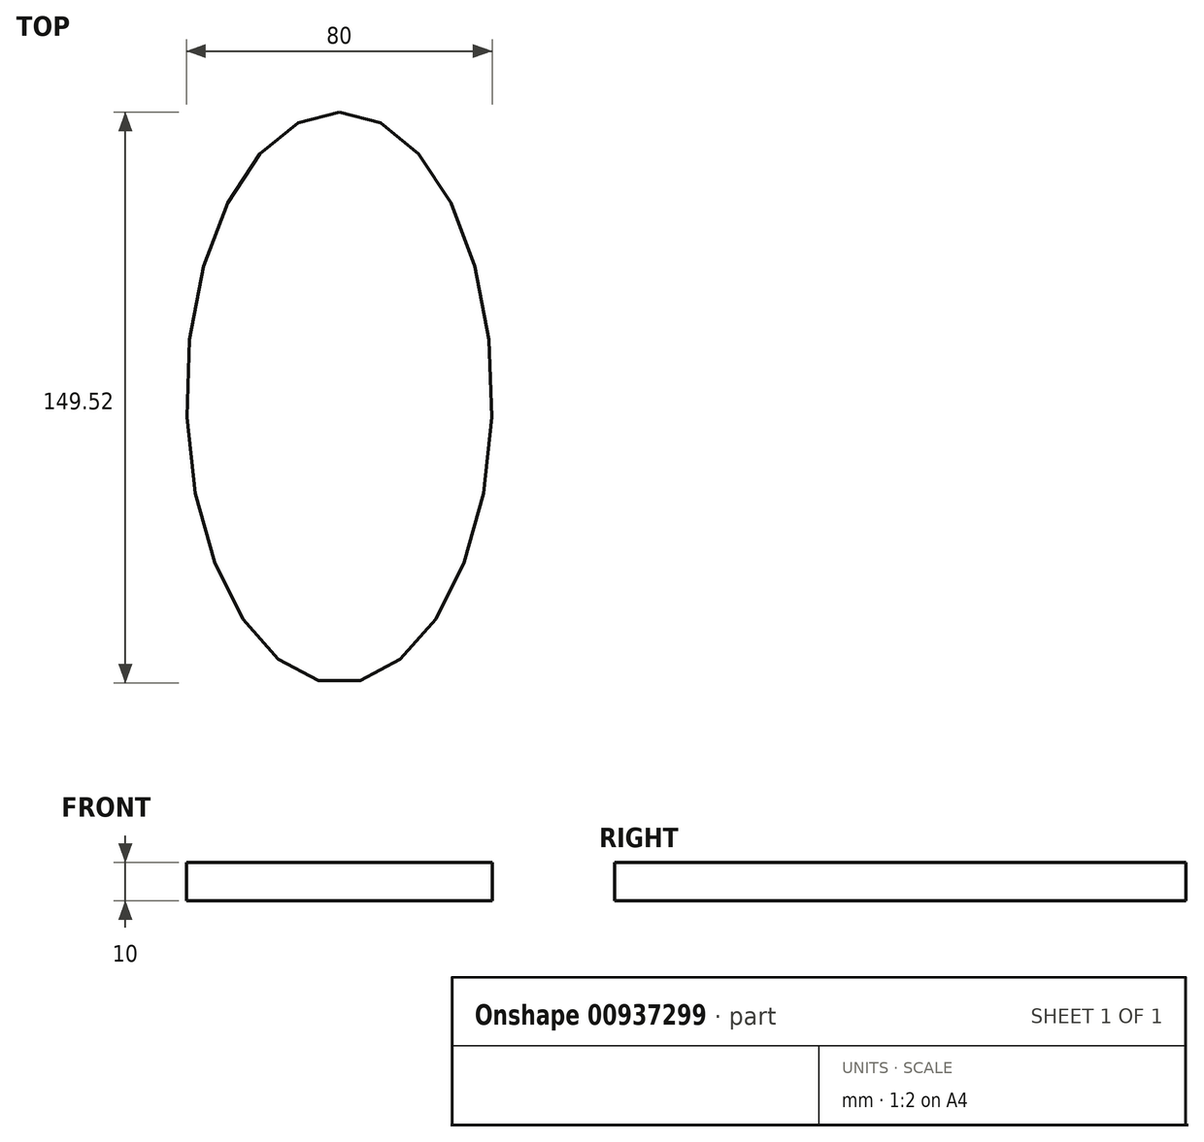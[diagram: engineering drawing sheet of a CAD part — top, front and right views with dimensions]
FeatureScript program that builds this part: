
annotation { "Feature Type Name" : "Feature", "Feature Type Description" : "" }
export const myFeature = defineFeature(function(context is Context, id is Id, definition is map)
    precondition{}
    {
        {
            var Q0;
            Q0=qCreatedBy(makeId("Top.planeOp"),FACE);
            var sketch = newSketch(context, id + "F0", { "sketchPlane" : qUnion([Q0])});
            skEllipse(sketch, "E0", {"center": v(0, 0) * mm, "majorRadius": 74.76 * mm, "minorRadius": 40 * mm, "majorAxis": v(0, 1)});
            skSolve(sketch);
        }
        {
            var Q0;
            Q0=makeQuery(id+"F0.imprint","IMPRINT",FACE,{"disambiguationData":[TD([[makeQuery(id+"F0.imprint","IMPRINT",EDGE,{"derivedFrom":sQuery(id+"F0.wireOp",EDGE,"E0")}),1.0]])]});
            extrude(context, id + "F1", {"entities" : qUnion([Q0]), "depth" : 10 * mm, "offsetDistance" : 25 * mm});
        }
    });
